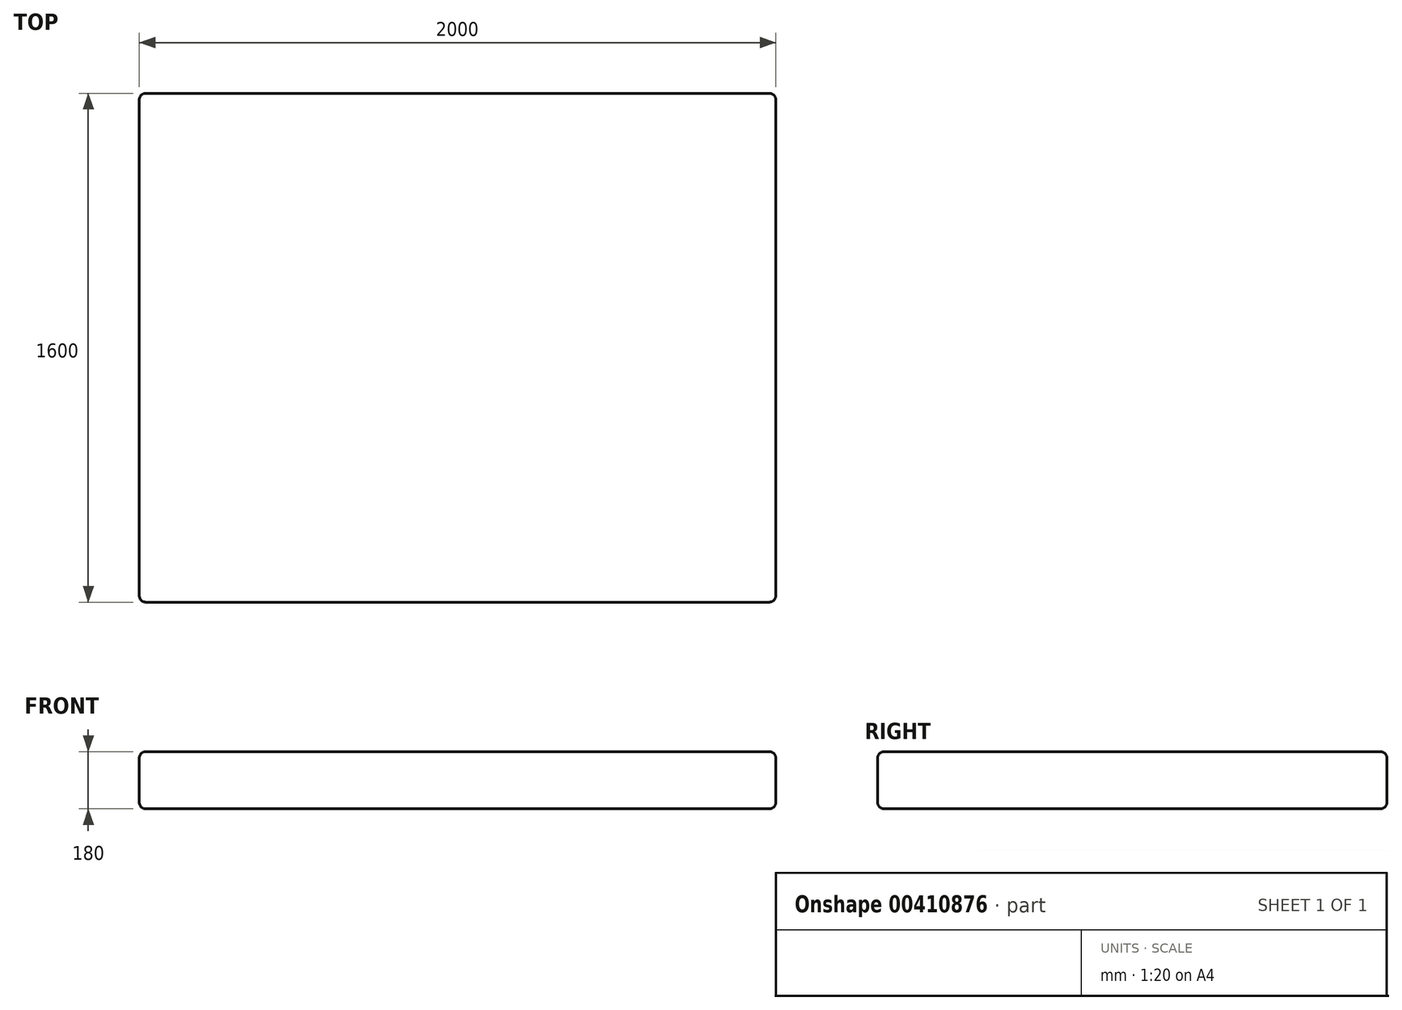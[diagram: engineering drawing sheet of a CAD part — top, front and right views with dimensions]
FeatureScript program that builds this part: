
annotation { "Feature Type Name" : "Feature", "Feature Type Description" : "" }
export const myFeature = defineFeature(function(context is Context, id is Id, definition is map)
    precondition{}
    {
        {
            var Q0;
            Q0=qCreatedBy(makeId("Top.planeOp"),FACE);
            var sketch = newSketch(context, id + "F0", { "sketchPlane" : qUnion([Q0])});
            skLineSegment(sketch, "E0.bottom", {"start": v(0, 0) * mm, "end": v(2000, 0) * mm});
            skLineSegment(sketch, "E0.top", {"start": v(0, -1600) * mm, "end": v(2000, -1600) * mm});
            skLineSegment(sketch, "E0.left", {"start": v(0, 0) * mm, "end": v(0, -1600) * mm});
            skLineSegment(sketch, "E0.right", {"start": v(2000, 0) * mm, "end": v(2000, -1600) * mm});
            skSolve(sketch);
        }
        {
            var Q0;
            Q0 = qSketchRegion(id + "F0", true);
            extrude(context, id + "F1", {"entities" : qUnion([Q0]), "depth" : 180 * mm, "offsetDistance" : 25 * mm});
        }
        {
            var Q0;
            Q0=makeQuery(id+"F1.opExtrude","CAP_EDGE",EDGE,{"disambiguationData":[OSD([sQuery(id+"F0.wireOp",EDGE,"E0.right")])],"isStart":false});
            var Q1;
            Q1=makeQuery(id+"F1.opExtrude","CAP_EDGE",EDGE,{"disambiguationData":[OSD([sQuery(id+"F0.wireOp",EDGE,"E0.top")])],"isStart":false});
            var Q2;
            Q2=makeQuery(id+"F1.opExtrude","CAP_EDGE",EDGE,{"disambiguationData":[OSD([sQuery(id+"F0.wireOp",EDGE,"E0.right")])],"isStart":true});
            var Q3;
            Q3=makeQuery(id+"F1.opExtrude","SWEPT_EDGE",EDGE,{"disambiguationData":[OSD([sQuery(id+"F0.wireOp",EDGE,"E0.top"),sQuery(id+"F0.wireOp",EDGE,"E0.right")])]});
            var Q4;
            Q4=makeQuery(id+"F1.opExtrude","CAP_EDGE",EDGE,{"disambiguationData":[OSD([sQuery(id+"F0.wireOp",EDGE,"E0.top")])],"isStart":true});
            var Q5;
            Q5=makeQuery(id+"F1.opExtrude","SWEPT_EDGE",EDGE,{"disambiguationData":[OSD([sQuery(id+"F0.wireOp",EDGE,"E0.bottom"),sQuery(id+"F0.wireOp",EDGE,"E0.right")])]});
            var Q6;
            Q6=makeQuery(id+"F1.opExtrude","CAP_EDGE",EDGE,{"disambiguationData":[OSD([sQuery(id+"F0.wireOp",EDGE,"E0.bottom")])],"isStart":false});
            var Q7;
            Q7=makeQuery(id+"F1.opExtrude","CAP_EDGE",EDGE,{"disambiguationData":[OSD([sQuery(id+"F0.wireOp",EDGE,"E0.bottom")])],"isStart":true});
            var Q8;
            Q8=makeQuery(id+"F1.opExtrude","CAP_EDGE",EDGE,{"disambiguationData":[OSD([sQuery(id+"F0.wireOp",EDGE,"E0.left")])],"isStart":false});
            var Q9;
            Q9=makeQuery(id+"F1.opExtrude","CAP_EDGE",EDGE,{"disambiguationData":[OSD([sQuery(id+"F0.wireOp",EDGE,"E0.left")])],"isStart":true});
            var Q10;
            Q10=makeQuery(id+"F1.opExtrude","SWEPT_EDGE",EDGE,{"disambiguationData":[OSD([sQuery(id+"F0.wireOp",EDGE,"E0.top"),sQuery(id+"F0.wireOp",EDGE,"E0.left")])]});
            var Q11;
            Q11=makeQuery(id+"F1.opExtrude","SWEPT_EDGE",EDGE,{"disambiguationData":[OSD([sQuery(id+"F0.wireOp",EDGE,"E0.bottom"),sQuery(id+"F0.wireOp",EDGE,"E0.left")])]});
            fillet(context, id + "F2", {"entities" : qUnion([Q0, Q1, Q2, Q3, Q4, Q5, Q6, Q7, Q8, Q9, Q10, Q11]), "radius" : 20 * mm, "tangentPropagation" : true, "allowEdgeOverflow" : false});
        }
    });
